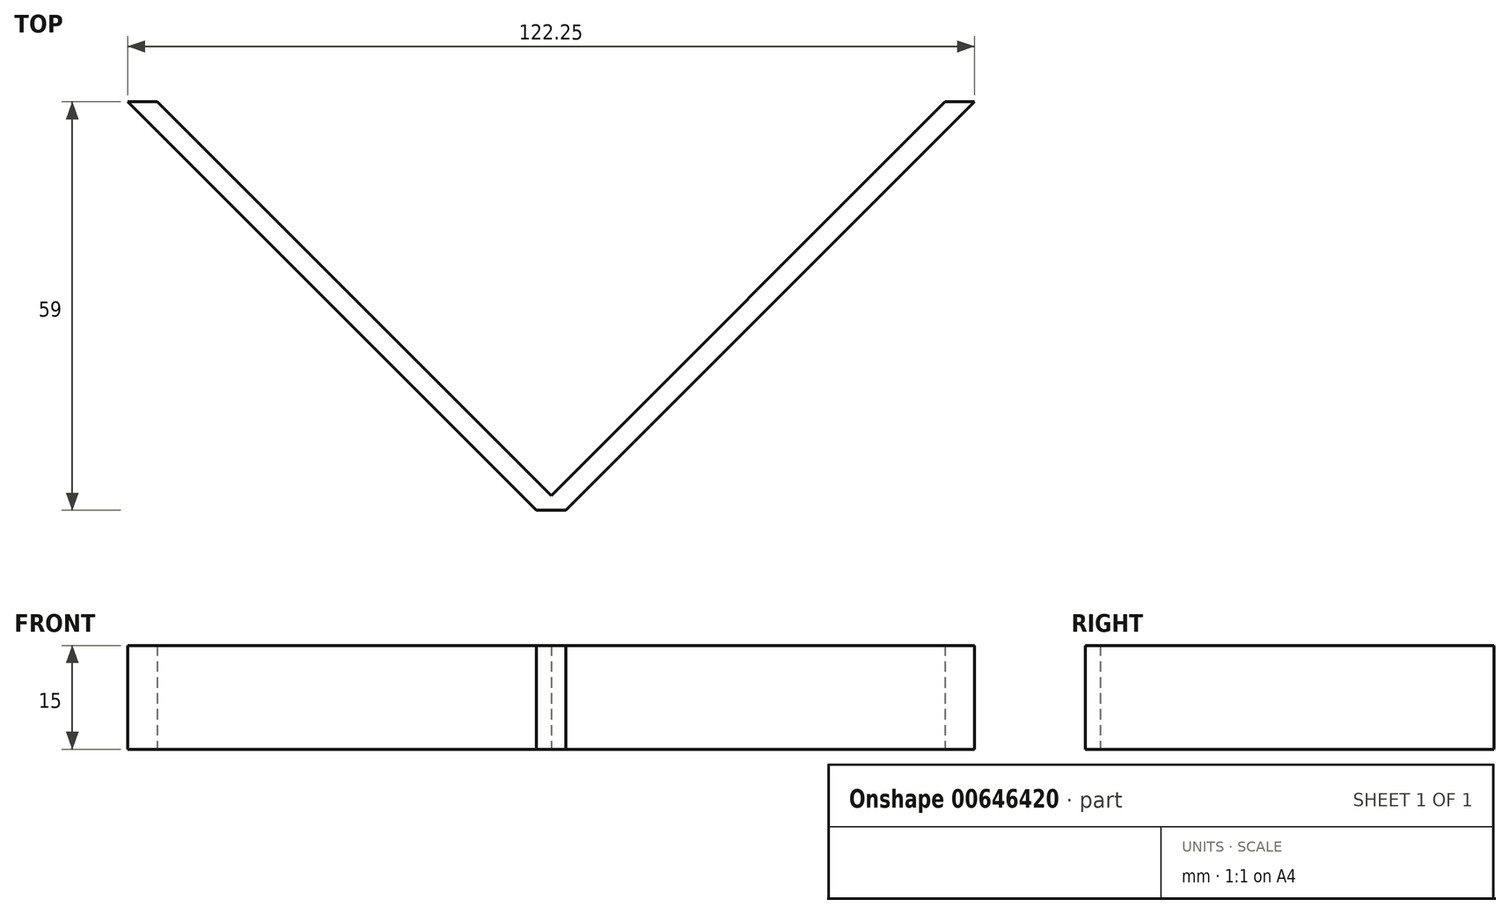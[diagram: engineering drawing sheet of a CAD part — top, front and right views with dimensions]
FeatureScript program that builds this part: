
annotation { "Feature Type Name" : "Feature", "Feature Type Description" : "" }
export const myFeature = defineFeature(function(context is Context, id is Id, definition is map)
    precondition{}
    {
        {
            var Q0;
            Q0=qCreatedBy(makeId("Top.planeOp"),FACE);
            var sketch = newSketch(context, id + "F0", { "sketchPlane" : qUnion([Q0])});
            skLineSegment(sketch, "E0.bottom", {"start": v(0, 0) * mm, "end": v(150, 0) * mm, "construction": true});
            skLineSegment(sketch, "E0.top", {"start": v(0, 59) * mm, "end": v(150, 59) * mm, "construction": true});
            skLineSegment(sketch, "E0.left", {"start": v(0, 0) * mm, "end": v(0, 59) * mm, "construction": true});
            skLineSegment(sketch, "E0.right", {"start": v(150, 0) * mm, "end": v(150, 59) * mm, "construction": true});
            skLineSegment(sketch, "E1", {"start": v(10.32, 59) * mm, "end": v(69.32, 0) * mm, "construction": true});
            skLineSegment(sketch, "E2", {"start": v(69.32, 0) * mm, "end": v(128.32, 59) * mm, "construction": true});
            skLineSegment(sketch, "E3", {"start": v(69.32, 2.12) * mm, "end": v(126.2, 59) * mm});
            skLineSegment(sketch, "E4", {"start": v(69.32, 2.12) * mm, "end": v(12.45, 59) * mm});
            skLineSegment(sketch, "E5", {"start": v(67.2, 0) * mm, "end": v(8.2, 59) * mm});
            skLineSegment(sketch, "E6", {"start": v(71.45, 0) * mm, "end": v(130.45, 59) * mm});
            skLineSegment(sketch, "E7", {"start": v(8.2, 59) * mm, "end": v(12.45, 59) * mm});
            skLineSegment(sketch, "E8", {"start": v(126.2, 59) * mm, "end": v(130.45, 59) * mm});
            skLineSegment(sketch, "E9", {"start": v(67.2, 0) * mm, "end": v(71.45, 0) * mm});
            skSolve(sketch);
        }
        {
            var Q0;
            Q0=makeQuery(id+"F0.imprint","IMPRINT",FACE,{"disambiguationData":[TD([[makeQuery(id+"F0.imprint","IMPRINT",EDGE,{"derivedFrom":sQuery(id+"F0.wireOp",EDGE,"E3")}),-1.0]])]});
            extrude(context, id + "F1", {"entities" : qUnion([Q0]), "depth" : 15 * mm, "offsetDistance" : 25 * mm});
        }
    });
